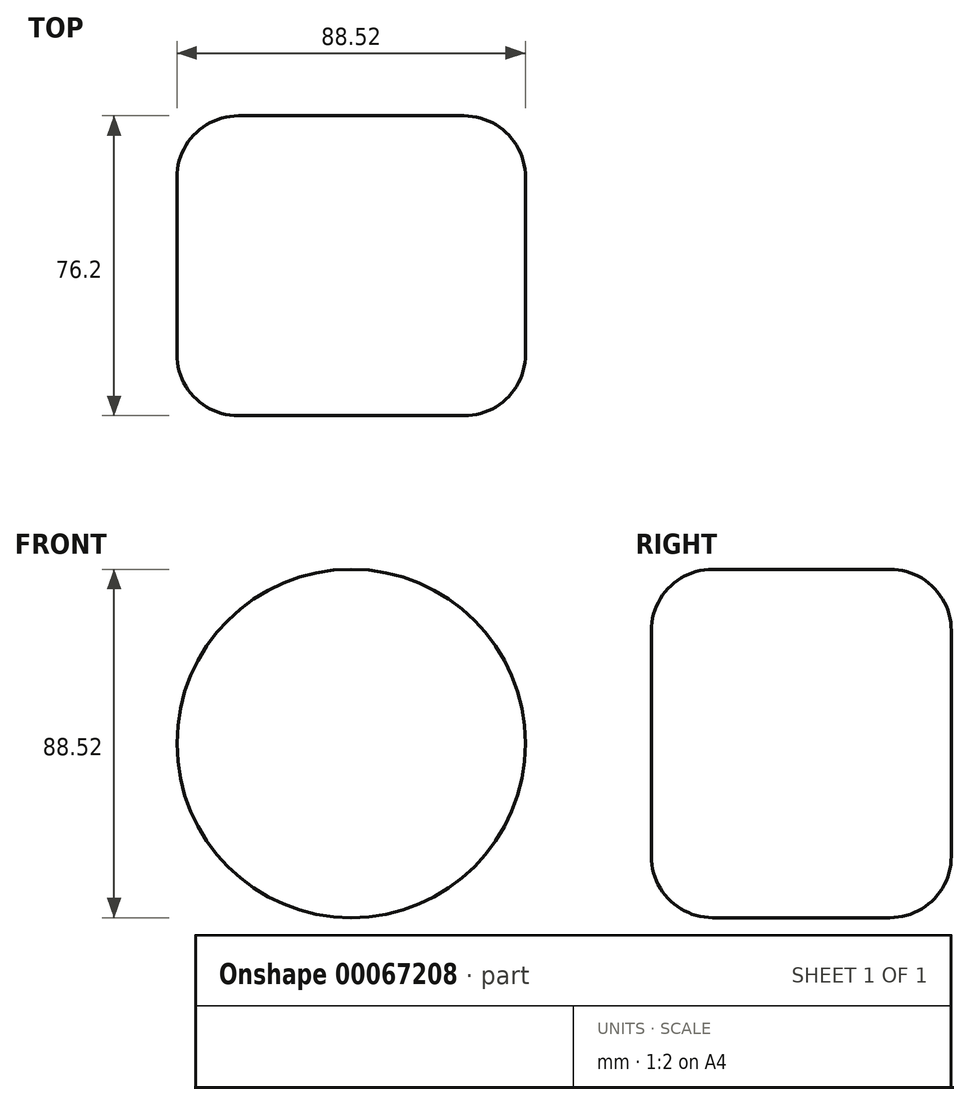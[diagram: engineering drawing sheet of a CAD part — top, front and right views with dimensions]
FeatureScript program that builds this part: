
annotation { "Feature Type Name" : "Feature", "Feature Type Description" : "" }
export const myFeature = defineFeature(function(context is Context, id is Id, definition is map)
    precondition{}
    {
        {
            var Q0;
            Q0=qCreatedBy(makeId("Front.planeOp"),FACE);
            var sketch = newSketch(context, id + "F0", { "sketchPlane" : qUnion([Q0])});
            skCircle(sketch, "E0", {"center": v(0, 0) * mm, "radius": 44.26 * mm});
            skCircle(sketch, "E1", {"center": v(118.94, 53.27) * mm, "radius": 14.02 * mm});
            skSolve(sketch);
        }
        {
            var Q0;
            Q0=makeQuery(id+"F0.imprint","IMPRINT",FACE,{"disambiguationData":[TD([[makeQuery(id+"F0.imprint","IMPRINT",EDGE,{"derivedFrom":sQuery(id+"F0.wireOp",EDGE,"E0")}),1.0]])]});
            extrude(context, id + "F1", {"entities" : qUnion([Q0]), "depth" : 76.2 * mm});
        }
        {
            var Q0;
            Q0=makeQuery(id+"F1.opExtrude","CAP_EDGE",EDGE,{"disambiguationData":[OSD([sQuery(id+"F0.wireOp",EDGE,"E0")])],"isStart":true});
            fillet(context, id + "F2", {"entities" : qUnion([Q0]), "radius" : 15.6 * mm, "tangentPropagation" : true, "allowEdgeOverflow" : false});
        }
        {
            var Q0;
            Q0=makeQuery(id+"F1.opExtrude","CAP_EDGE",EDGE,{"disambiguationData":[OSD([sQuery(id+"F0.wireOp",EDGE,"E0")])],"isStart":false});
            fillet(context, id + "F3", {"entities" : qUnion([Q0]), "radius" : 15.58 * mm, "tangentPropagation" : true, "allowEdgeOverflow" : false});
        }
    });
